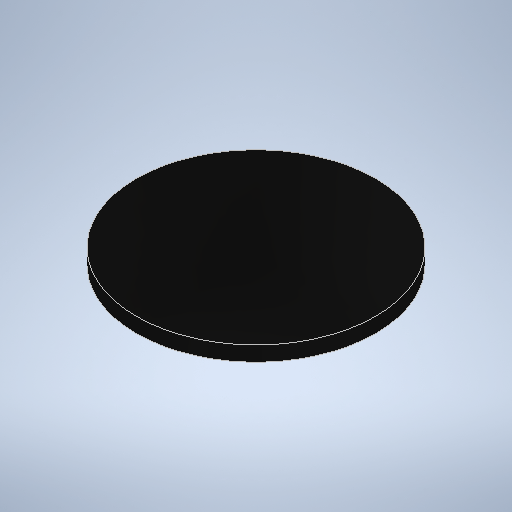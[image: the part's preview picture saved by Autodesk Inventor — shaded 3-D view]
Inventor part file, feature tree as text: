
AUTODESK INVENTOR PART (.ipt)
format: ipt  version: 2025.2 (Build 292293000, 293)  size: 219,136 bytes
history: native  units: mm
features: other x1, extrude x1, sketch x1
ambient origin geometry x8: Origin, YZ Plane, XZ Plane, XY Plane, X Axis, Y Axis, Z Axis, Center Point
bodies: Body1 (feature_tree)
feature tree (3):
  other  "ソリッド1"
  extrude  "押し出し1"  Depth=8.0mm
  sketch  "スケッチ1"
